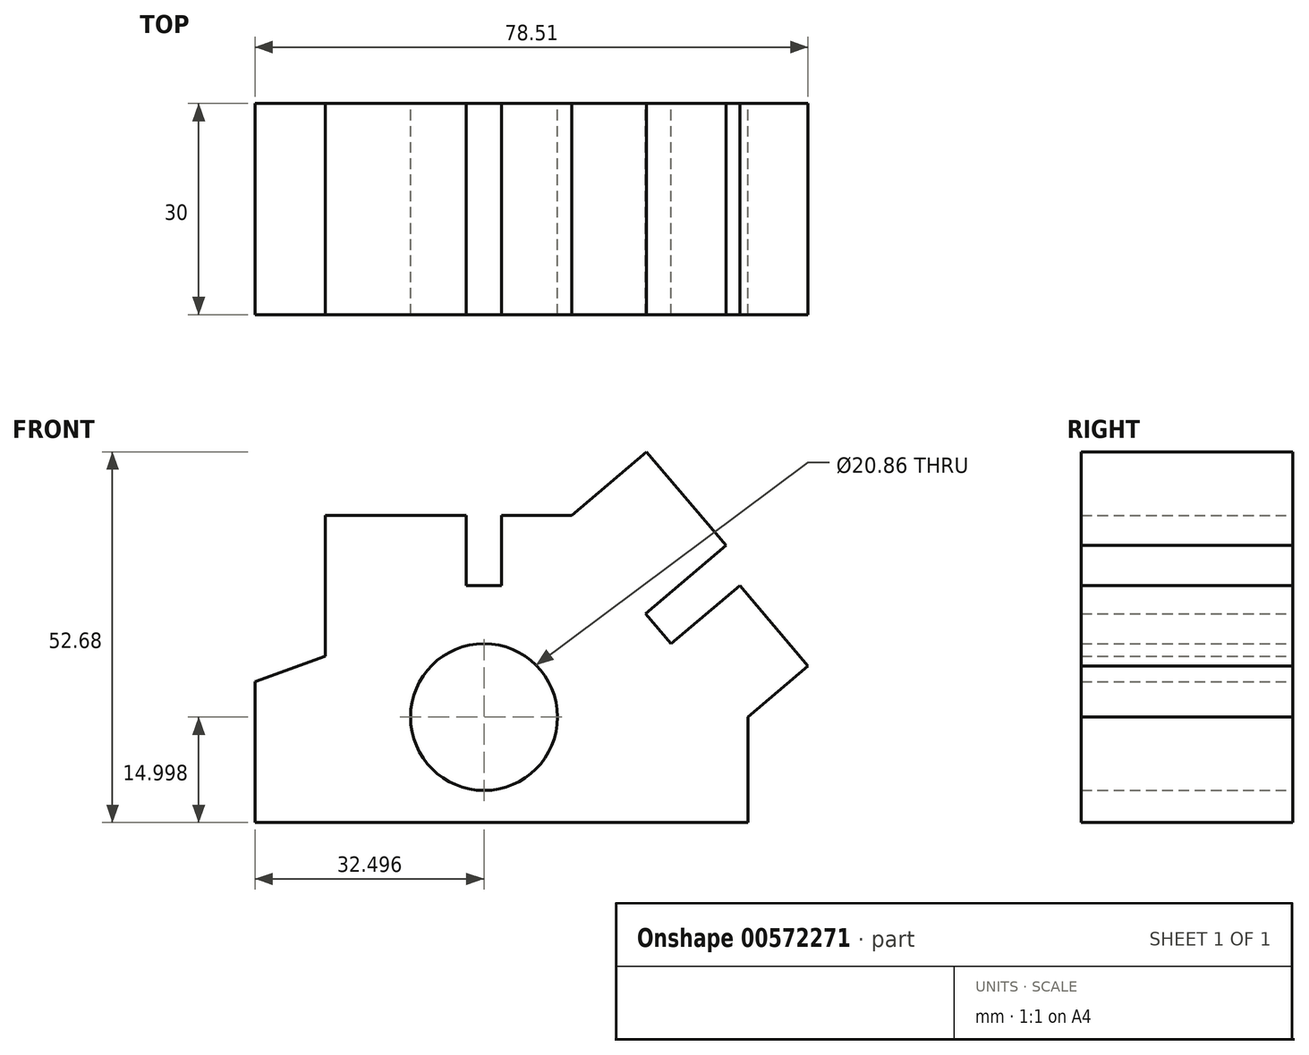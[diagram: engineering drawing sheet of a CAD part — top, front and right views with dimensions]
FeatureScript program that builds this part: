
annotation { "Feature Type Name" : "Feature", "Feature Type Description" : "" }
export const myFeature = defineFeature(function(context is Context, id is Id, definition is map)
    precondition{}
    {
        {
            var Q0;
            Q0=qCreatedBy(makeId("Front.planeOp"),FACE);
            var sketch = newSketch(context, id + "F0", { "sketchPlane" : qUnion([Q0])});
            skLineSegment(sketch, "E0", {"start": v(-53.31, -43.25) * mm, "end": v(16.69, -43.25) * mm});
            skLineSegment(sketch, "E1", {"start": v(16.69, -43.25) * mm, "end": v(16.69, -28.25) * mm});
            skLineSegment(sketch, "E2", {"start": v(16.69, -28.25) * mm, "end": v(25.2, -21.01) * mm});
            skLineSegment(sketch, "E3", {"start": v(25.2, -21.01) * mm, "end": v(15.49, -9.58) * mm});
            skPoint(sketch, "E4.end.orphan", {"position": v(2.12, -21.01) * mm});
            skLineSegment(sketch, "E5", {"start": v(15.49, -9.58) * mm, "end": v(5.77, -17.84) * mm});
            skLineSegment(sketch, "E6", {"start": v(5.77, -17.84) * mm, "end": v(2.12, -13.55) * mm});
            skLineSegment(sketch, "E7", {"start": v(2.12, -13.55) * mm, "end": v(13.55, -3.84) * mm});
            skLineSegment(sketch, "E8", {"start": v(13.55, -3.84) * mm, "end": v(2.27, 9.43) * mm});
            skLineSegment(sketch, "E9", {"start": v(2.27, 9.43) * mm, "end": v(-8.34, 0.42) * mm});
            skLineSegment(sketch, "E10", {"start": v(-8.34, 0.42) * mm, "end": v(-18.34, 0.42) * mm});
            skLineSegment(sketch, "E11", {"start": v(-18.34, 0.42) * mm, "end": v(-18.34, -9.58) * mm});
            skLineSegment(sketch, "E12", {"start": v(-18.34, -9.58) * mm, "end": v(-23.34, -9.58) * mm});
            skLineSegment(sketch, "E13", {"start": v(-23.34, -9.58) * mm, "end": v(-23.34, 0.42) * mm});
            skLineSegment(sketch, "E14", {"start": v(-23.34, 0.42) * mm, "end": v(-43.34, 0.42) * mm});
            skLineSegment(sketch, "E15", {"start": v(-43.34, 0.42) * mm, "end": v(-43.34, -19.58) * mm});
            skLineSegment(sketch, "E16", {"start": v(-53.31, -43.25) * mm, "end": v(-53.31, -23.25) * mm});
            skLineSegment(sketch, "E17", {"start": v(-53.31, -23.25) * mm, "end": v(-43.34, -19.58) * mm});
            skCircle(sketch, "E18", {"center": v(-20.81, -28.25) * mm, "radius": 10.43 * mm});
            skSolve(sketch);
        }
        {
            var Q0;
            Q0 = qSketchRegion(id + "F0", true);
            extrude(context, id + "F1", {"entities" : qUnion([Q0]), "depth" : 30 * mm, "offsetDistance" : 25 * mm});
        }
    });
